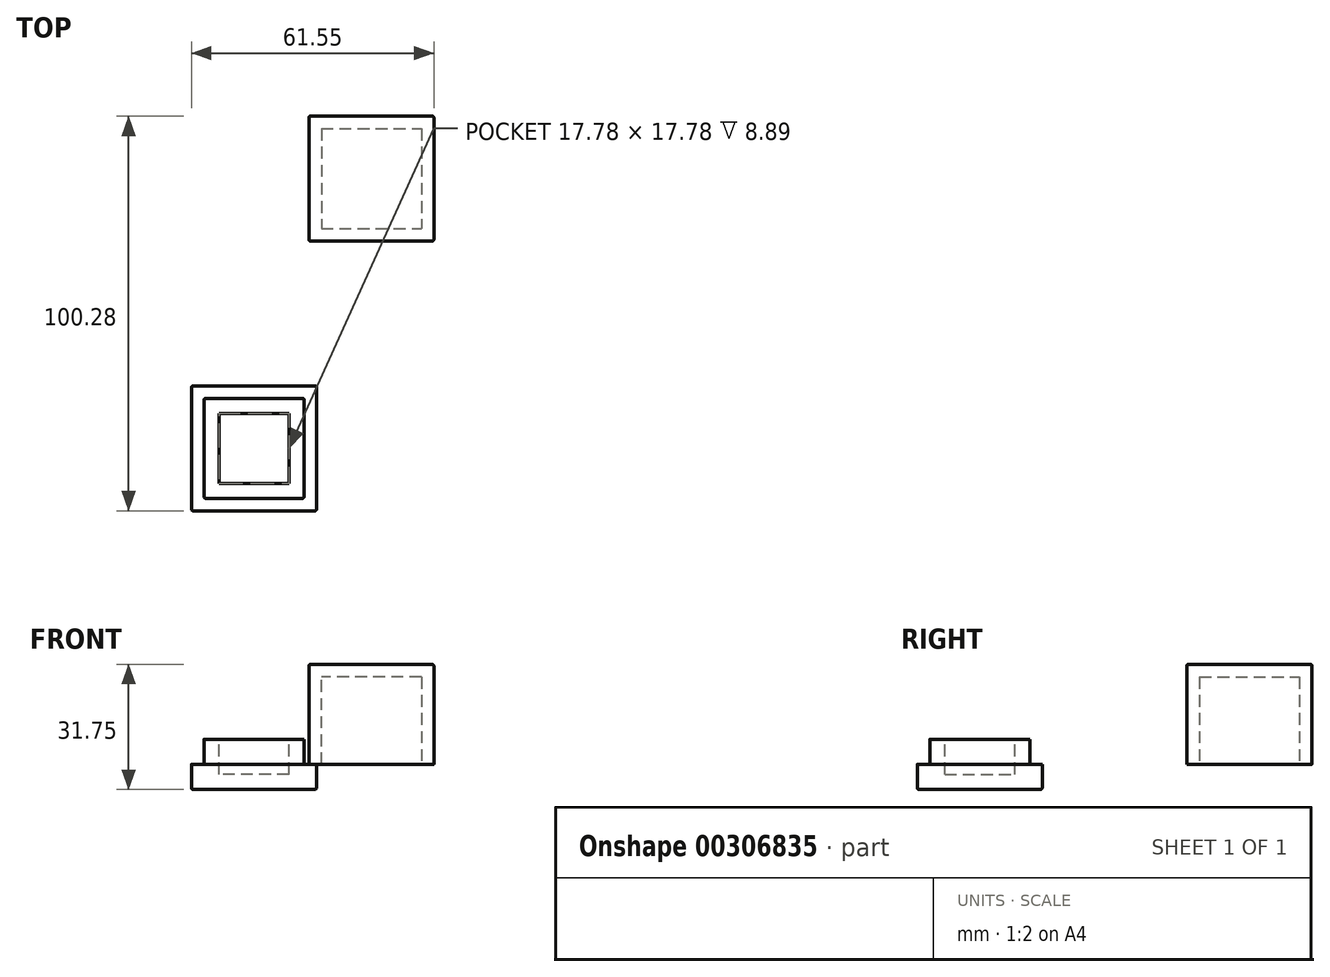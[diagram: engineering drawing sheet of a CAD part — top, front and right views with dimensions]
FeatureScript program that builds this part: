
annotation { "Feature Type Name" : "Feature", "Feature Type Description" : "" }
export const myFeature = defineFeature(function(context is Context, id is Id, definition is map)
    precondition{}
    {
        {
            var Q0;
            Q0=qCreatedBy(makeId("Top.planeOp"),FACE);
            var sketch = newSketch(context, id + "F0", { "sketchPlane" : qUnion([Q0])});
            skLineSegment(sketch, "E0.bottom", {"start": v(0, 0) * mm, "end": v(31.75, 0) * mm});
            skLineSegment(sketch, "E0.top", {"start": v(0, -31.75) * mm, "end": v(31.75, -31.75) * mm});
            skLineSegment(sketch, "E0.left", {"start": v(0, 0) * mm, "end": v(0, -31.75) * mm});
            skLineSegment(sketch, "E0.right", {"start": v(31.75, 0) * mm, "end": v(31.75, -31.75) * mm});
            skSolve(sketch);
        }
        {
            var Q0;
            Q0=makeQuery(id+"F0.imprint","IMPRINT",FACE,{"disambiguationData":[TD([[makeQuery(id+"F0.imprint","IMPRINT",EDGE,{"derivedFrom":sQuery(id+"F0.wireOp",EDGE,"E0.bottom")}),-1.0]])]});
            extrude(context, id + "F1", {"entities" : qUnion([Q0]), "depth" : 25.4 * mm});
        }
        {
            var Q0;
            Q0=makeQuery(id+"F1.opExtrude","SWEPT_EDGE",EDGE,{"disambiguationData":[OSD([sQuery(id+"F0.wireOp",EDGE,"E0.bottom"),sQuery(id+"F0.wireOp",EDGE,"E0.right")])]});
            var Q1;
            Q1=makeQuery(id+"F1.opExtrude","CAP_EDGE",EDGE,{"disambiguationData":[OSD([sQuery(id+"F0.wireOp",EDGE,"E0.bottom")])],"isStart":false});
            var Q2;
            Q2=makeQuery(id+"F1.opExtrude","CAP_EDGE",EDGE,{"disambiguationData":[OSD([sQuery(id+"F0.wireOp",EDGE,"E0.right")])],"isStart":false});
            var Q3;
            Q3=makeQuery(id+"F1.opExtrude","CAP_EDGE",EDGE,{"disambiguationData":[OSD([sQuery(id+"F0.wireOp",EDGE,"E0.top")])],"isStart":false});
            var Q4;
            Q4=makeQuery(id+"F1.opExtrude","CAP_EDGE",EDGE,{"disambiguationData":[OSD([sQuery(id+"F0.wireOp",EDGE,"E0.left")])],"isStart":false});
            var Q5;
            Q5=makeQuery(id+"F1.opExtrude","SWEPT_EDGE",EDGE,{"disambiguationData":[OSD([sQuery(id+"F0.wireOp",EDGE,"E0.bottom"),sQuery(id+"F0.wireOp",EDGE,"E0.left")])]});
            var Q6;
            Q6=makeQuery(id+"F1.opExtrude","SWEPT_EDGE",EDGE,{"disambiguationData":[OSD([sQuery(id+"F0.wireOp",EDGE,"E0.top"),sQuery(id+"F0.wireOp",EDGE,"E0.left")])]});
            var Q7;
            Q7=makeQuery(id+"F1.opExtrude","SWEPT_EDGE",EDGE,{"disambiguationData":[OSD([sQuery(id+"F0.wireOp",EDGE,"E0.top"),sQuery(id+"F0.wireOp",EDGE,"E0.right")])]});
            fillet(context, id + "F2", {"entities" : qUnion([Q0, Q1, Q2, Q3, Q4, Q5, Q6, Q7]), "radius" : 0.38 * mm, "tangentPropagation" : true, "allowEdgeOverflow" : false});
        }
        {
            var Q0;
            Q0=qCreatedBy(makeId("Top.planeOp"),FACE);
            var sketch = newSketch(context, id + "F3", { "sketchPlane" : qUnion([Q0])});
            skLineSegment(sketch, "E1.bottom", {"start": v(-29.8, -68.53) * mm, "end": v(1.95, -68.53) * mm});
            skLineSegment(sketch, "E1.top", {"start": v(-29.8, -100.28) * mm, "end": v(1.95, -100.28) * mm});
            skLineSegment(sketch, "E1.left", {"start": v(-29.8, -68.53) * mm, "end": v(-29.8, -100.28) * mm});
            skLineSegment(sketch, "E1.right", {"start": v(1.95, -68.53) * mm, "end": v(1.95, -100.28) * mm});
            skSolve(sketch);
        }
        {
            var Q0;
            Q0=makeQuery(id+"F3.imprint","IMPRINT",FACE,{"disambiguationData":[TD([[makeQuery(id+"F3.imprint","IMPRINT",EDGE,{"derivedFrom":sQuery(id+"F3.wireOp",EDGE,"E1.bottom")}),-1.0]])]});
            extrude(context, id + "F4", {"entities" : qUnion([Q0]), "oppositeDirection" : true, "depth" : 6.35 * mm});
        }
        {
            var Q0;
            Q0=makeQuery(id+"F4.opExtrude","SWEPT_EDGE",EDGE,{"disambiguationData":[OSD([sQuery(id+"F3.wireOp",EDGE,"E1.top"),sQuery(id+"F3.wireOp",EDGE,"E1.right")])]});
            var Q1;
            Q1=makeQuery(id+"F4.opExtrude","SWEPT_EDGE",EDGE,{"disambiguationData":[OSD([sQuery(id+"F3.wireOp",EDGE,"E1.top"),sQuery(id+"F3.wireOp",EDGE,"E1.left")])]});
            var Q2;
            Q2=makeQuery(id+"F4.opExtrude","CAP_EDGE",EDGE,{"disambiguationData":[OSD([sQuery(id+"F3.wireOp",EDGE,"E1.top")])],"isStart":false});
            var Q3;
            Q3=makeQuery(id+"F4.opExtrude","CAP_EDGE",EDGE,{"disambiguationData":[OSD([sQuery(id+"F3.wireOp",EDGE,"E1.left")])],"isStart":false});
            var Q4;
            Q4=makeQuery(id+"F4.opExtrude","CAP_EDGE",EDGE,{"disambiguationData":[OSD([sQuery(id+"F3.wireOp",EDGE,"E1.bottom")])],"isStart":false});
            var Q5;
            Q5=makeQuery(id+"F4.opExtrude","SWEPT_EDGE",EDGE,{"disambiguationData":[OSD([sQuery(id+"F3.wireOp",EDGE,"E1.bottom"),sQuery(id+"F3.wireOp",EDGE,"E1.left")])]});
            var Q6;
            Q6=makeQuery(id+"F4.opExtrude","SWEPT_EDGE",EDGE,{"disambiguationData":[OSD([sQuery(id+"F3.wireOp",EDGE,"E1.bottom"),sQuery(id+"F3.wireOp",EDGE,"E1.right")])]});
            var Q7;
            Q7=makeQuery(id+"F4.opExtrude","CAP_EDGE",EDGE,{"disambiguationData":[OSD([sQuery(id+"F3.wireOp",EDGE,"E1.right")])],"isStart":false});
            fillet(context, id + "F5", {"entities" : qUnion([Q0, Q1, Q2, Q3, Q4, Q5, Q6, Q7]), "radius" : 0.38 * mm, "tangentPropagation" : true, "allowEdgeOverflow" : false});
        }
        {
            var Q0;
            Q0=makeQuery(id+"F1.opExtrude","CAP_FACE",FACE,{"disambiguationData":[OSD([sQuery(id+"F0.wireOp",EDGE,"E0.bottom"),sQuery(id+"F0.wireOp",EDGE,"E0.top"),sQuery(id+"F0.wireOp",EDGE,"E0.left"),sQuery(id+"F0.wireOp",EDGE,"E0.right")])],"isStart":true});
            shell(context, id + "F6", {"entities" : qUnion([Q0]), "thickness" : 3.17 * mm});
        }
        {
            var Q0;
            Q0=makeQuery(id+"F4.opExtrude","CAP_FACE",FACE,{"disambiguationData":[OSD([sQuery(id+"F3.wireOp",EDGE,"E1.bottom"),sQuery(id+"F3.wireOp",EDGE,"E1.top"),sQuery(id+"F3.wireOp",EDGE,"E1.left"),sQuery(id+"F3.wireOp",EDGE,"E1.right")])],"isStart":true});
            var sketch = newSketch(context, id + "F7", { "sketchPlane" : qUnion([Q0])});
            skLineSegment(sketch, "E2.bottom", {"start": v(-26.62, -71.7) * mm, "end": v(-1.22, -71.7) * mm});
            skLineSegment(sketch, "E2.top", {"start": v(-26.62, -97.1) * mm, "end": v(-1.22, -97.1) * mm});
            skLineSegment(sketch, "E2.left", {"start": v(-26.62, -71.7) * mm, "end": v(-26.62, -97.1) * mm});
            skLineSegment(sketch, "E2.right", {"start": v(-1.22, -71.7) * mm, "end": v(-1.22, -97.1) * mm});
            skSolve(sketch);
        }
        {
            var Q0;
            Q0=makeQuery(id+"F7.imprint","IMPRINT",FACE,{"disambiguationData":[TD([[makeQuery(id+"F7.imprint","IMPRINT",EDGE,{"derivedFrom":sQuery(id+"F7.wireOp",EDGE,"E2.bottom")}),-1.0]])]});
            extrude(context, id + "F8", {"entities" : qUnion([Q0]), "operationType" : NewBodyOperationType.ADD, "depth" : 6.35 * mm});
        }
        {
            var Q0;
            Q0=makeQuery(id+"F8.opExtrude","SWEPT_EDGE",EDGE,{"disambiguationData":[OSD([sQuery(id+"F7.wireOp",EDGE,"E2.bottom"),sQuery(id+"F7.wireOp",EDGE,"E2.left")])]});
            var Q1;
            Q1=makeQuery(id+"F8.opExtrude","SWEPT_EDGE",EDGE,{"disambiguationData":[OSD([sQuery(id+"F7.wireOp",EDGE,"E2.top"),sQuery(id+"F7.wireOp",EDGE,"E2.left")])]});
            var Q2;
            Q2=makeQuery(id+"F8.opExtrude","SWEPT_EDGE",EDGE,{"disambiguationData":[OSD([sQuery(id+"F7.wireOp",EDGE,"E2.top"),sQuery(id+"F7.wireOp",EDGE,"E2.right")])]});
            var Q3;
            Q3=makeQuery(id+"F8.opExtrude","SWEPT_EDGE",EDGE,{"disambiguationData":[OSD([sQuery(id+"F7.wireOp",EDGE,"E2.bottom"),sQuery(id+"F7.wireOp",EDGE,"E2.right")])]});
            fillet(context, id + "F9", {"entities" : qUnion([Q0, Q1, Q2, Q3]), "radius" : 0.4 * mm, "tangentPropagation" : true, "allowEdgeOverflow" : false});
        }
        {
            var Q0;
            Q0=makeQuery(id+"F8.opExtrude","CAP_FACE",FACE,{"disambiguationData":[OSD([sQuery(id+"F7.wireOp",EDGE,"E2.bottom"),sQuery(id+"F7.wireOp",EDGE,"E2.top"),sQuery(id+"F7.wireOp",EDGE,"E2.left"),sQuery(id+"F7.wireOp",EDGE,"E2.right")])],"isStart":false});
            shell(context, id + "F10", {"entities" : qUnion([Q0]), "thickness" : 3.8 * mm});
        }
    });
